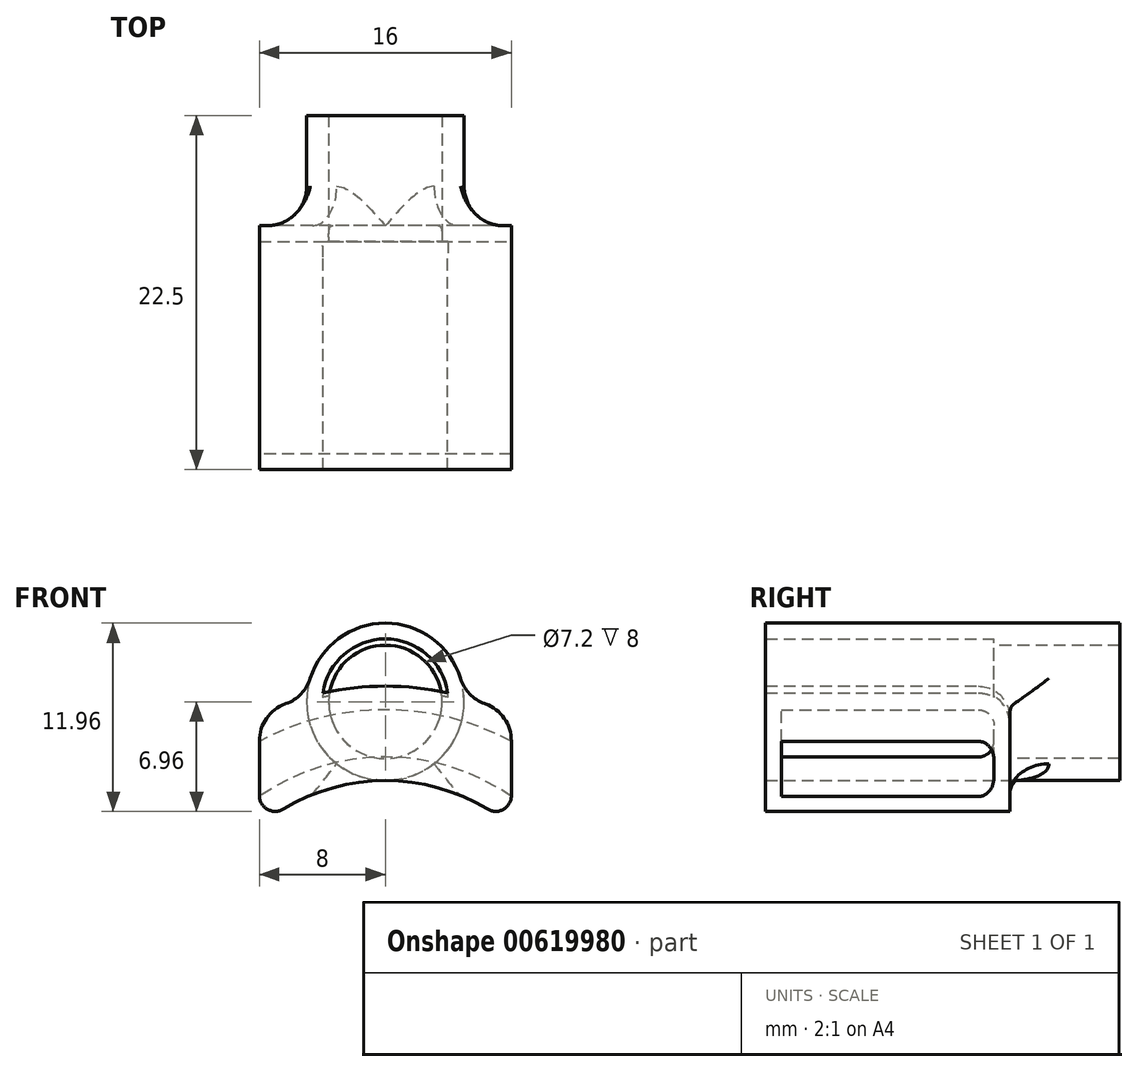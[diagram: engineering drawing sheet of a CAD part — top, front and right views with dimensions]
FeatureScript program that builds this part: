
annotation { "Feature Type Name" : "Feature", "Feature Type Description" : "" }
export const myFeature = defineFeature(function(context is Context, id is Id, definition is map)
    precondition{}
    {
        {
            var Q0;
            Q0=qCreatedBy(makeId("Front.planeOp"),FACE);
            var sketch = newSketch(context, id + "F0", { "sketchPlane" : qUnion([Q0])});
            skArc(sketch, "E0", {"start": v(8, 9.6) * mm, "mid": v(0, 12.5) * mm, "end": v(-8, 9.6) * mm});
            skArc(sketch, "E1.0", {"start": v(8, 11.49) * mm, "mid": v(0, 14) * mm, "end": v(-8, 11.49) * mm});
            skLineSegment(sketch, "E2", {"start": v(-8, 11.49) * mm, "end": v(-8, 9.6) * mm});
            skLineSegment(sketch, "E3", {"start": v(8, 11.49) * mm, "end": v(8, 9.6) * mm});
            skArc(sketch, "E4.0", {"start": v(8, 15) * mm, "mid": v(0, 17) * mm, "end": v(-8, 15) * mm});
            skLineSegment(sketch, "E5", {"start": v(-8, 15) * mm, "end": v(-8, 16.68) * mm});
            skLineSegment(sketch, "E6", {"start": v(8, 15) * mm, "end": v(8, 16.68) * mm});
            skArc(sketch, "E7.0", {"start": v(8, 16.68) * mm, "mid": v(0, 18.5) * mm, "end": v(-8, 16.68) * mm});
            skPoint(sketch, "E8.end.orphan", {"position": v(-8, 29.56) * mm});
            skPoint(sketch, "E8.start.orphan", {"position": v(8, 29.56) * mm});
            skArc(sketch, "E9", {"start": v(5, 17.81) * mm, "mid": v(0, 22.5) * mm, "end": v(-5, 17.81) * mm});
            skPoint(sketch, "E9.centerSnap0", {"position": v(0, 17) * mm});
            skArc(sketch, "E10.0", {"start": v(3.96, 18.07) * mm, "mid": v(0, 21.5) * mm, "end": v(-3.96, 18.07) * mm});
            skSolve(sketch);
        }
        {
            var Q0;
            Q0=qSketchRegion(id+"F0",true);
            extrude(context, id + "F1", {"entities" : qUnion([Q0]), "depth" : 13.5 * mm, "offsetDistance" : 25 * mm});
        }
        {
            var Q0;
            Q0=makeQuery(id+"F1.opExtrude","CAP_FACE",FACE,{"disambiguationData":[OSD([sQuery(id+"F0.wireOp",EDGE,"E0"),sQuery(id+"F0.wireOp",EDGE,"E1.0"),sQuery(id+"F0.wireOp",EDGE,"E2"),sQuery(id+"F0.wireOp",EDGE,"E3")])],"isStart":true});
            var sketch = newSketch(context, id + "F2", { "sketchPlane" : qUnion([Q0])});
            skCircle(sketch, "E11", {"center": v(0, 17.5) * mm, "radius": 3.6 * mm});
            skPoint(sketch, "E11.centerSnap0", {"position": v(0, 14) * mm});
            skCircle(sketch, "E12", {"center": v(0, 17.5) * mm, "radius": 5 * mm});
            skSolve(sketch);
        }
        {
            var Q0;
            Q0 = qSketchRegion(id + "F2", true);
            extrude(context, id + "F3", {"entities" : qUnion([Q0]), "depth" : 8 * mm, "offsetDistance" : 25 * mm});
        }
        {
            var Q0;
            Q0=makeQuery(id+"F1.opExtrude","CAP_FACE",FACE,{"disambiguationData":[OSD([sQuery(id+"F0.wireOp",EDGE,"E4.0"),sQuery(id+"F0.wireOp",EDGE,"E5"),sQuery(id+"F0.wireOp",EDGE,"E6"),sQuery(id+"F0.wireOp",EDGE,"E7.0"),sQuery(id+"F0.wireOp",EDGE,"E9"),sQuery(id+"F0.wireOp",EDGE,"E10.0")])],"isStart":true});
            var sketch = newSketch(context, id + "F4", { "sketchPlane" : qUnion([Q0])});
            skArc(sketch, "E13.0", {"start": v(-3.54, 18.16) * mm, "mid": v(0, 13.9) * mm, "end": v(3.54, 18.16) * mm});
            skArc(sketch, "E14.0", {"start": v(-3.54, 18.16) * mm, "mid": v(0, 18.5) * mm, "end": v(3.54, 18.16) * mm});
            skSolve(sketch);
        }
        {
            var Q0;
            Q0 = qSketchRegion(id + "F4", true);
            extrude(context, id + "F5", {"entities" : qUnion([Q0]), "depth" : 1 * mm, "offsetDistance" : 25 * mm});
        }
        {
            var Q0;
            Q0=makeQuery(id+"F1.opExtrude","CAP_FACE",FACE,{"disambiguationData":[OSD([sQuery(id+"F0.wireOp",EDGE,"E0"),sQuery(id+"F0.wireOp",EDGE,"E1.0"),sQuery(id+"F0.wireOp",EDGE,"E2"),sQuery(id+"F0.wireOp",EDGE,"E3")])],"isStart":true});
            var sketch = newSketch(context, id + "F6", { "sketchPlane" : qUnion([Q0])});
            skLineSegment(sketch, "E15.0", {"start": v(-8, 11.49) * mm, "end": v(-8, 9.6) * mm});
            skLineSegment(sketch, "E15.2", {"start": v(8, 9.6) * mm, "end": v(8, 11.49) * mm});
            skArc(sketch, "E15.3", {"start": v(-8, 9.6) * mm, "mid": v(0, 12.5) * mm, "end": v(8, 9.6) * mm});
            skArc(sketch, "E16.0", {"start": v(-8, 16.68) * mm, "mid": v(-6.52, 17.31) * mm, "end": v(-5, 17.81) * mm});
            skArc(sketch, "E17.0", {"start": v(5, 17.81) * mm, "mid": v(6.52, 17.31) * mm, "end": v(8, 16.68) * mm});
            skLineSegment(sketch, "E18.0", {"start": v(-8, 15) * mm, "end": v(-8, 16.68) * mm});
            skLineSegment(sketch, "E19.0", {"start": v(8, 15) * mm, "end": v(8, 16.68) * mm});
            skArc(sketch, "E20.0", {"start": v(-5, 17.81) * mm, "mid": v(0, 12.5) * mm, "end": v(5, 17.81) * mm});
            skLineSegment(sketch, "E21", {"start": v(-8, 15) * mm, "end": v(-8, 11.49) * mm});
            skLineSegment(sketch, "E22", {"start": v(8, 15) * mm, "end": v(8, 11.49) * mm});
            skSolve(sketch);
        }
        {
            var Q0;
            Q0 = qSketchRegion(id + "F6", true);
            extrude(context, id + "F7", {"entities" : qUnion([Q0]), "depth" : 1 * mm, "offsetDistance" : 25 * mm});
        }
        {
            var Q0;
            Q0=makeQuery(id+"F1.opExtrude","CAP_FACE",FACE,{"disambiguationData":[OSD([sQuery(id+"F0.wireOp",EDGE,"E0"),sQuery(id+"F0.wireOp",EDGE,"E1.0"),sQuery(id+"F0.wireOp",EDGE,"E2"),sQuery(id+"F0.wireOp",EDGE,"E3")])],"isStart":false});
            var sketch = newSketch(context, id + "F8", { "sketchPlane" : qUnion([Q0])});
            skArc(sketch, "E23.0", {"start": v(8, 9.6) * mm, "mid": v(0, 12.5) * mm, "end": v(-8, 9.6) * mm});
            skArc(sketch, "E24.0", {"start": v(8, 16.68) * mm, "mid": v(0, 18.5) * mm, "end": v(-8, 16.68) * mm});
            skLineSegment(sketch, "E25", {"start": v(-8, 9.6) * mm, "end": v(-8, 16.68) * mm});
            skLineSegment(sketch, "E26", {"start": v(8, 9.6) * mm, "end": v(8, 16.68) * mm});
            skArc(sketch, "E27.0", {"start": v(5, 17.81) * mm, "mid": v(0, 22.5) * mm, "end": v(-5, 17.81) * mm});
            skArc(sketch, "E28.0", {"start": v(3.96, 18.07) * mm, "mid": v(0, 21.5) * mm, "end": v(-3.96, 18.07) * mm});
            skSolve(sketch);
        }
        {
            var Q0;
            Q0 = qSketchRegion(id + "F8", true);
            extrude(context, id + "F9", {"entities" : qUnion([Q0]), "depth" : 1 * mm, "offsetDistance" : 25 * mm});
        }
        {
            var Q0;
            Q0=makeQuery(id+"F1.opExtrude","SWEPT_BODY",BODY,{"disambiguationData":[OSD([sQuery(id+"F0.wireOp",EDGE,"E4.0"),sQuery(id+"F0.wireOp",EDGE,"E5"),sQuery(id+"F0.wireOp",EDGE,"E6"),sQuery(id+"F0.wireOp",EDGE,"E7.0"),sQuery(id+"F0.wireOp",EDGE,"E9"),sQuery(id+"F0.wireOp",EDGE,"E10.0")])]});
            var Q1;
            Q1=makeQuery(id+"F3.opExtrude","SWEPT_BODY",BODY,{"disambiguationData":[OSD([sQuery(id+"F2.wireOp",EDGE,"E11"),sQuery(id+"F2.wireOp",EDGE,"E12")])]});
            var Q2;
            Q2=makeQuery(id+"F1.opExtrude","SWEPT_BODY",BODY,{"disambiguationData":[OSD([sQuery(id+"F0.wireOp",EDGE,"E0"),sQuery(id+"F0.wireOp",EDGE,"E1.0"),sQuery(id+"F0.wireOp",EDGE,"E2"),sQuery(id+"F0.wireOp",EDGE,"E3")])]});
            var Q3;
            Q3=makeQuery(id+"F7.opExtrude","SWEPT_BODY",BODY,{"disambiguationData":[OSD([sQuery(id+"F6.wireOp",EDGE,"E15.2"),sQuery(id+"F6.wireOp",EDGE,"E15.3"),sQuery(id+"F6.wireOp",EDGE,"E17.0"),sQuery(id+"F6.wireOp",EDGE,"E19.0"),sQuery(id+"F6.wireOp",EDGE,"E20.0"),sQuery(id+"F6.wireOp",EDGE,"E22")])]});
            var Q4;
            Q4=makeQuery(id+"F7.opExtrude","SWEPT_BODY",BODY,{"disambiguationData":[OSD([sQuery(id+"F6.wireOp",EDGE,"E15.0"),sQuery(id+"F6.wireOp",EDGE,"E15.3"),sQuery(id+"F6.wireOp",EDGE,"E16.0"),sQuery(id+"F6.wireOp",EDGE,"E18.0"),sQuery(id+"F6.wireOp",EDGE,"E20.0"),sQuery(id+"F6.wireOp",EDGE,"E21")])]});
            var Q5;
            Q5=makeQuery(id+"F5.opExtrude","SWEPT_BODY",BODY,{"disambiguationData":[OSD([sQuery(id+"F4.wireOp",EDGE,"E13.0"),sQuery(id+"F4.wireOp",EDGE,"E14.0")])]});
            var Q6;
            Q6=makeQuery(id+"F9.opExtrude","SWEPT_BODY",BODY,{"disambiguationData":[OSD([sQuery(id+"F8.wireOp",EDGE,"E23.0"),sQuery(id+"F8.wireOp",EDGE,"E24.0"),sQuery(id+"F8.wireOp",EDGE,"E25"),sQuery(id+"F8.wireOp",EDGE,"E26")])]});
            booleanBodies(context, id + "F10", {"operationType" : BooleanOperationType.UNION, "tools" : qUnion([Q0, Q1, Q2, Q3, Q4, Q5, Q6])});
        }
        {
            var Q0;
            Q0=makeQuery(id+"F5.opExtrude","CAP_EDGE",EDGE,{"disambiguationData":[OSD([sQuery(id+"F4.wireOp",EDGE,"E14.0")])],"isStart":false});
            fillet(context, id + "F11", {"entities" : qUnion([Q0]), "radius" : 2 * mm, "tangentPropagation" : true, "allowEdgeOverflow" : false});
        }
        {
            var Q0;
            {var subQ0=sQuery(id+"F0.wireOp",EDGE,"E9");var subQ1=sQuery(id+"F0.wireOp",EDGE,"E7.0");Q0=makeQuery(id+"F10.opBoolean","MERGE",EDGE,{"derivedFrom":[makeQuery(id+"F1.opExtrude","SWEPT_EDGE",EDGE,{"disambiguationData":[OSD([subQ1,subQ0]),TDD([makeQuery(id+"F0.imprint","INTERSECT",VERTEX,{"disambiguationData":[OD(1.0)],"derivedFrom":[subQ1,subQ0]})])]}),makeQuery(id+"F7.opExtrude","SWEPT_EDGE",EDGE,{"disambiguationData":[OSD([sQuery(id+"F6.wireOp",EDGE,"E17.0"),sQuery(id+"F6.wireOp",EDGE,"E20.0")])]})]});}
            var Q1;
            Q1=makeQuery(id+"F10.opBoolean","MERGE",EDGE,{"derivedFrom":[makeQuery(id+"F1.opExtrude","SWEPT_EDGE",EDGE,{"disambiguationData":[OSD([sQuery(id+"F0.wireOp",EDGE,"E5"),sQuery(id+"F0.wireOp",EDGE,"E7.0")])]}),makeQuery(id+"F7.opExtrude","SWEPT_EDGE",EDGE,{"disambiguationData":[OSD([sQuery(id+"F6.wireOp",EDGE,"E17.0"),sQuery(id+"F6.wireOp",EDGE,"E19.0")])]}),makeQuery(id+"F9.opExtrude","SWEPT_EDGE",EDGE,{"disambiguationData":[OSD([sQuery(id+"F8.wireOp",EDGE,"E24.0"),sQuery(id+"F8.wireOp",EDGE,"E25")])]})]});
            var Q2;
            {var subQ0=sQuery(id+"F0.wireOp",EDGE,"E9");var subQ1=sQuery(id+"F0.wireOp",EDGE,"E7.0");Q2=makeQuery(id+"F10.opBoolean","MERGE",EDGE,{"derivedFrom":[makeQuery(id+"F1.opExtrude","SWEPT_EDGE",EDGE,{"disambiguationData":[OSD([subQ1,subQ0]),TDD([makeQuery(id+"F0.imprint","INTERSECT",VERTEX,{"disambiguationData":[OD(0.0)],"derivedFrom":[subQ1,subQ0]})])]}),makeQuery(id+"F7.opExtrude","SWEPT_EDGE",EDGE,{"disambiguationData":[OSD([sQuery(id+"F6.wireOp",EDGE,"E16.0"),sQuery(id+"F6.wireOp",EDGE,"E20.0")])]})]});}
            var Q3;
            Q3=makeQuery(id+"F10.opBoolean","MERGE",EDGE,{"derivedFrom":[makeQuery(id+"F1.opExtrude","SWEPT_EDGE",EDGE,{"disambiguationData":[OSD([sQuery(id+"F0.wireOp",EDGE,"E6"),sQuery(id+"F0.wireOp",EDGE,"E7.0")])]}),makeQuery(id+"F7.opExtrude","SWEPT_EDGE",EDGE,{"disambiguationData":[OSD([sQuery(id+"F6.wireOp",EDGE,"E16.0"),sQuery(id+"F6.wireOp",EDGE,"E18.0")])]}),makeQuery(id+"F9.opExtrude","SWEPT_EDGE",EDGE,{"disambiguationData":[OSD([sQuery(id+"F8.wireOp",EDGE,"E24.0"),sQuery(id+"F8.wireOp",EDGE,"E26")])]})]});
            fillet(context, id + "F12", {"entities" : qUnion([Q0, Q1, Q2, Q3]), "radius" : 2.5 * mm, "tangentPropagation" : true, "allowEdgeOverflow" : false});
        }
        {
            var Q0;
            {var subQ0=sQuery(id+"F6.wireOp",EDGE,"E20.0");Q0=makeQuery(id+"F7.opExtrude","CAP_EDGE",EDGE,{"disambiguationData":[OSD([subQ0]),TDD([makeQuery(id+"F6.imprint","IMPRINT",EDGE,{"disambiguationData":[TD([[makeQuery(id+"F6.imprint","INTERSECT",VERTEX,{"derivedFrom":[sQuery(id+"F6.wireOp",EDGE,"E15.3"),subQ0]}),-1.0]])],"derivedFrom":subQ0}),makeQuery(id+"F6.imprint","IMPRINT",EDGE,{"disambiguationData":[TD([[makeQuery(id+"F6.imprint","INTERSECT",VERTEX,{"derivedFrom":[sQuery(id+"F6.wireOp",EDGE,"E17.0"),subQ0]}),1.0]])],"derivedFrom":subQ0})])],"isStart":false});}
            fillet(context, id + "F13", {"entities" : qUnion([Q0]), "radius" : 2.5 * mm, "tangentPropagation" : true, "allowEdgeOverflow" : false});
        }
        {
            var Q0;
            Q0=makeQuery(id+"F10.opBoolean","MERGE",EDGE,{"derivedFrom":[makeQuery(id+"F1.opExtrude","SWEPT_EDGE",EDGE,{"disambiguationData":[OSD([sQuery(id+"F0.wireOp",EDGE,"E0"),sQuery(id+"F0.wireOp",EDGE,"E2")])]}),makeQuery(id+"F7.opExtrude","SWEPT_EDGE",EDGE,{"disambiguationData":[OSD([sQuery(id+"F6.wireOp",EDGE,"E15.2"),sQuery(id+"F6.wireOp",EDGE,"E15.3")])]}),makeQuery(id+"F9.opExtrude","SWEPT_EDGE",EDGE,{"disambiguationData":[OSD([sQuery(id+"F8.wireOp",EDGE,"E23.0"),sQuery(id+"F8.wireOp",EDGE,"E25")])]})]});
            var Q1;
            Q1=makeQuery(id+"F10.opBoolean","MERGE",EDGE,{"derivedFrom":[makeQuery(id+"F1.opExtrude","SWEPT_EDGE",EDGE,{"disambiguationData":[OSD([sQuery(id+"F0.wireOp",EDGE,"E0"),sQuery(id+"F0.wireOp",EDGE,"E3")])]}),makeQuery(id+"F7.opExtrude","SWEPT_EDGE",EDGE,{"disambiguationData":[OSD([sQuery(id+"F6.wireOp",EDGE,"E15.0"),sQuery(id+"F6.wireOp",EDGE,"E15.3")])]}),makeQuery(id+"F9.opExtrude","SWEPT_EDGE",EDGE,{"disambiguationData":[OSD([sQuery(id+"F8.wireOp",EDGE,"E23.0"),sQuery(id+"F8.wireOp",EDGE,"E26")])]})]});
            fillet(context, id + "F14", {"entities" : qUnion([Q0, Q1]), "radius" : 1 * mm, "tangentPropagation" : true, "allowEdgeOverflow" : false});
        }
        {
            var Q0;
            {var subQ0=sQuery(id+"F6.wireOp",EDGE,"E20.0");var subQ1=sQuery(id+"F6.wireOp",EDGE,"E15.3");Q0=makeQuery(id+"F10.opBoolean","INTERSECT",EDGE,{"derivedFrom":[makeQuery(id+"F3.opExtrude","CAP_FACE",FACE,{"disambiguationData":[OSD([sQuery(id+"F2.wireOp",EDGE,"E11"),sQuery(id+"F2.wireOp",EDGE,"E12")])],"isStart":true}),makeQuery(id+"F5.opExtrude","CAP_FACE",FACE,{"disambiguationData":[OSD([sQuery(id+"F4.wireOp",EDGE,"E13.0"),sQuery(id+"F4.wireOp",EDGE,"E14.0")])],"isStart":true}),makeQuery(id+"F7.opExtrude","CAP_FACE",FACE,{"disambiguationData":[OSD([sQuery(id+"F6.wireOp",EDGE,"E15.0"),subQ1,sQuery(id+"F6.wireOp",EDGE,"E16.0"),sQuery(id+"F6.wireOp",EDGE,"E18.0"),subQ0,sQuery(id+"F6.wireOp",EDGE,"E21")])],"isStart":true}),makeQuery(id+"F7.opExtrude","CAP_FACE",FACE,{"disambiguationData":[OSD([sQuery(id+"F6.wireOp",EDGE,"E15.2"),subQ1,sQuery(id+"F6.wireOp",EDGE,"E17.0"),sQuery(id+"F6.wireOp",EDGE,"E19.0"),subQ0,sQuery(id+"F6.wireOp",EDGE,"E22")])],"isStart":true})]});}
            var Q1;
            Q1=makeQuery(id+"F1.opExtrude","CAP_EDGE",EDGE,{"disambiguationData":[OSD([sQuery(id+"F0.wireOp",EDGE,"E4.0")])],"isStart":true});
            var Q2;
            Q2=makeQuery(id+"F1.opExtrude","CAP_EDGE",EDGE,{"disambiguationData":[OSD([sQuery(id+"F0.wireOp",EDGE,"E1.0")])],"isStart":false});
            var Q3;
            Q3=makeQuery(id+"F1.opExtrude","CAP_EDGE",EDGE,{"disambiguationData":[OSD([sQuery(id+"F0.wireOp",EDGE,"E4.0")])],"isStart":false});
            fillet(context, id + "F15", {"entities" : qUnion([Q0, Q1, Q2, Q3]), "radius" : 1 * mm, "tangentPropagation" : true, "allowEdgeOverflow" : false});
        }
    });
